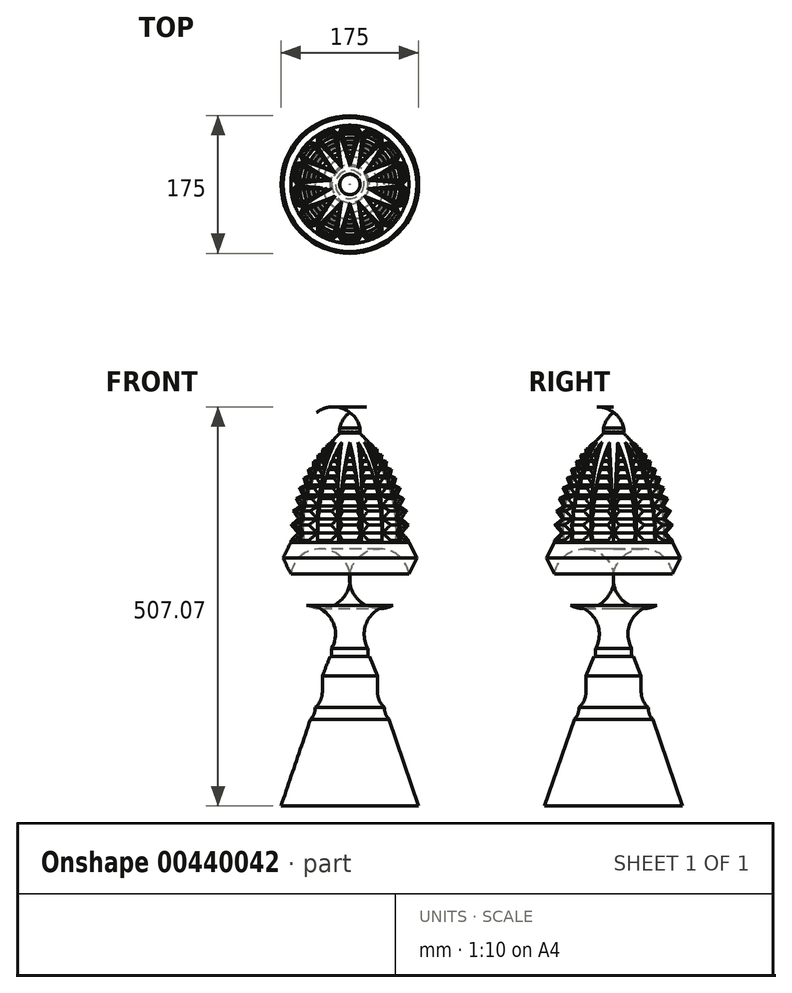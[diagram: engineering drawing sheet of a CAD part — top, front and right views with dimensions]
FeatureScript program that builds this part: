
annotation { "Feature Type Name" : "Feature", "Feature Type Description" : "" }
export const myFeature = defineFeature(function(context is Context, id is Id, definition is map)
    precondition{}
    {
        {
            var Q0;
            Q0=qCreatedBy(makeId("Front.planeOp"),FACE);
            var sketch = newSketch(context, id + "F0", { "sketchPlane" : qUnion([Q0])});
            skLineSegment(sketch, "E0", {"start": v(0, 0) * mm, "end": v(87.5, 0) * mm});
            skLineSegment(sketch, "E1", {"start": v(0, 0) * mm, "end": v(0, 110) * mm});
            skLineSegment(sketch, "E2", {"start": v(0, 110) * mm, "end": v(50, 110) * mm});
            skLineSegment(sketch, "E3", {"start": v(50, 110) * mm, "end": v(87.5, 0) * mm});
            skLineSegment(sketch, "E4", {"start": v(-407.4, 0) * mm, "end": v(-407.4, 108) * mm});
            skLineSegment(sketch, "E5", {"start": v(-453.78, 108) * mm, "end": v(-352.64, 108) * mm});
            skLineSegment(sketch, "E6", {"start": v(-407.4, 108) * mm, "end": v(-407.4, 123) * mm});
            skLineSegment(sketch, "E7", {"start": v(-407.4, 123) * mm, "end": v(-407.4, 143) * mm});
            skLineSegment(sketch, "E8", {"start": v(0, 110) * mm, "end": v(0, 125) * mm});
            skLineSegment(sketch, "E9", {"start": v(0, 125) * mm, "end": v(0, 145) * mm});
            skLineSegment(sketch, "E10", {"start": v(-446.66, 122.59) * mm, "end": v(-359.68, 122.59) * mm});
            skLineSegment(sketch, "E11", {"start": v(0, 125) * mm, "end": v(44, 125) * mm});
            skLineSegment(sketch, "E12", {"start": v(-438.63, 143) * mm, "end": v(-367.86, 143) * mm});
            skLineSegment(sketch, "E13", {"start": v(0, 145) * mm, "end": v(35, 145) * mm});
            skArc(sketch, "E14", {"start": v(35, 145) * mm, "mid": v(37.38, 134.05) * mm, "end": v(44, 125) * mm});
            skArc(sketch, "E15", {"start": v(44, 125) * mm, "mid": v(45.42, 116.87) * mm, "end": v(50, 110) * mm});
            skLineSegment(sketch, "E16", {"start": v(-407.4, 143) * mm, "end": v(-407.4, 188) * mm});
            skLineSegment(sketch, "E17", {"start": v(-378.97, 188) * mm, "end": v(-428.97, 188) * mm});
            skLineSegment(sketch, "E18", {"start": v(-407.4, 188) * mm, "end": v(-407.4, 198) * mm});
            skLineSegment(sketch, "E19", {"start": v(0, 145) * mm, "end": v(0, 190) * mm});
            skLineSegment(sketch, "E20", {"start": v(-437.68, 163) * mm, "end": v(-367.68, 163) * mm});
            skLineSegment(sketch, "E21", {"start": v(0, 165) * mm, "end": v(35, 165) * mm, "construction": true});
            skLineSegment(sketch, "E22", {"start": v(35, 165) * mm, "end": v(35, 145) * mm});
            skLineSegment(sketch, "E23", {"start": v(0, 190) * mm, "end": v(25, 190) * mm});
            skLineSegment(sketch, "E24", {"start": v(25, 190) * mm, "end": v(35, 165) * mm});
            skLineSegment(sketch, "E25", {"start": v(-407.4, 198) * mm, "end": v(-407.4, 253) * mm});
            skLineSegment(sketch, "E26", {"start": v(-458.35, 253) * mm, "end": v(-348.35, 253) * mm});
            skLineSegment(sketch, "E27", {"start": v(0, 190) * mm, "end": v(0, 200) * mm});
            skLineSegment(sketch, "E28", {"start": v(0, 200) * mm, "end": v(23, 200) * mm});
            skLineSegment(sketch, "E29", {"start": v(-407.4, 253) * mm, "end": v(-407.4, 263) * mm});
            skLineSegment(sketch, "E30", {"start": v(23, 200) * mm, "end": v(23, 190) * mm});
            skLineSegment(sketch, "E31", {"start": v(0, 200) * mm, "end": v(0, 255) * mm});
            skLineSegment(sketch, "E32", {"start": v(0, 255) * mm, "end": v(55, 255) * mm});
            skArc(sketch, "E33", {"start": v(55, 255) * mm, "mid": v(23.18, 236.7) * mm, "end": v(23, 200) * mm});
            skLineSegment(sketch, "E34", {"start": v(-407.4, 263) * mm, "end": v(-407.4, 500) * mm});
            skLineSegment(sketch, "E35", {"start": v(-479.16, 303) * mm, "end": v(-329.16, 303) * mm});
            skLineSegment(sketch, "E36", {"start": v(-489.2, 323) * mm, "end": v(-319.2, 323) * mm});
            skPoint(sketch, "E37", {"position": v(-407.4, 303) * mm});
            skPoint(sketch, "E37.positionSnap0", {"position": v(-404.16, 303) * mm});
            skPoint(sketch, "E38", {"position": v(-407.4, 323) * mm});
            skPoint(sketch, "E38.positionSnap0", {"position": v(-404.2, 323) * mm});
            skLineSegment(sketch, "E39", {"start": v(0, 255) * mm, "end": v(0, 295) * mm});
            skLineSegment(sketch, "E40", {"start": v(0, 295) * mm, "end": v(0, 315) * mm});
            skLineSegment(sketch, "E41", {"start": v(0, 315) * mm, "end": v(0, 335) * mm});
            skLineSegment(sketch, "E42", {"start": v(0, 335) * mm, "end": v(0, 475) * mm});
            skLineSegment(sketch, "E43", {"start": v(0, 295) * mm, "end": v(75, 295) * mm});
            skLineSegment(sketch, "E44", {"start": v(0, 315) * mm, "end": v(85, 315) * mm});
            skLineSegment(sketch, "E45", {"start": v(85, 315) * mm, "end": v(75, 295) * mm});
            skArc(sketch, "E46", {"start": v(55, 255) * mm, "mid": v(71.5, 271.75) * mm, "end": v(75, 295) * mm});
            skPoint(sketch, "E47", {"position": v(-407.4, 343) * mm});
            skLineSegment(sketch, "E48", {"start": v(-407.4, 343) * mm, "end": v(-407.4, 483) * mm});
            skLineSegment(sketch, "E49", {"start": v(-478.01, 343) * mm, "end": v(-328.5, 343) * mm});
            skLineSegment(sketch, "E50", {"start": v(0, 335) * mm, "end": v(75, 335) * mm});
            skLineSegment(sketch, "E51", {"start": v(75, 335) * mm, "end": v(85, 315) * mm});
            skLineSegment(sketch, "E52", {"start": v(-416.64, 483) * mm, "end": v(-390.64, 483) * mm});
            skLineSegment(sketch, "E53", {"start": v(0, 475) * mm, "end": v(13, 475) * mm});
            skArc(sketch, "E54", {"start": v(75, 335) * mm, "mid": v(60.65, 412.38) * mm, "end": v(13, 475) * mm});
            skLineSegment(sketch, "E55", {"start": v(0, 475) * mm, "end": v(0, 500) * mm});
            skLineSegment(sketch, "E56", {"start": v(13, 475) * mm, "end": v(13, 480) * mm});
            skLineSegment(sketch, "E57", {"start": v(13, 480) * mm, "end": v(0, 480) * mm});
            skArc(sketch, "E58", {"start": v(13, 480) * mm, "mid": v(8.26, 491.14) * mm, "end": v(0, 500) * mm});
            skSolve(sketch);
        }
        {
            var Q0;
            {var subQ2=sQuery(id+"F0.wireOp",EDGE,"E57");Q0=makeQuery(id+"F0.imprint","IMPRINT",FACE,{"disambiguationData":[TD([[makeQuery(id+"F0.imprint","IMPRINT",EDGE,{"derivedFrom":subQ2}),-1.0]])]});}
            var Q1;
            Q1=makeQuery(id+"F0.imprint","IMPRINT",FACE,{"disambiguationData":[TD([[makeQuery(id+"F0.imprint","IMPRINT",EDGE,{"derivedFrom":sQuery(id+"F0.wireOp",EDGE,"E41")}),-1.0]])]});
            var Q2;
            Q2=makeQuery(id+"F0.imprint","IMPRINT",FACE,{"disambiguationData":[TD([[makeQuery(id+"F0.imprint","IMPRINT",EDGE,{"derivedFrom":sQuery(id+"F0.wireOp",EDGE,"E32")}),1.0]])]});
            var Q3;
            {var subQ0=sQuery(id+"F0.wireOp",EDGE,"E53");Q3=makeQuery(id+"F0.imprint","IMPRINT",FACE,{"disambiguationData":[TD([[makeQuery(id+"F0.imprint","IMPRINT",EDGE,{"derivedFrom":subQ0}),1.0]])]});}
            var Q4;
            Q4=makeQuery(id+"F0.imprint","IMPRINT",FACE,{"disambiguationData":[TD([[makeQuery(id+"F0.imprint","IMPRINT",EDGE,{"derivedFrom":sQuery(id+"F0.wireOp",EDGE,"E0")}),1.0]])]});
            var Q5;
            Q5=makeQuery(id+"F0.imprint","IMPRINT",FACE,{"disambiguationData":[TD([[makeQuery(id+"F0.imprint","IMPRINT",EDGE,{"derivedFrom":sQuery(id+"F0.wireOp",EDGE,"E9")}),-1.0]])]});
            var Q6;
            Q6=makeQuery(id+"F0.imprint","IMPRINT",FACE,{"disambiguationData":[TD([[makeQuery(id+"F0.imprint","IMPRINT",EDGE,{"derivedFrom":sQuery(id+"F0.wireOp",EDGE,"E13")}),1.0]])]});
            var Q7;
            {var subQ0=sQuery(id+"F0.wireOp",EDGE,"E27");Q7=makeQuery(id+"F0.imprint","IMPRINT",FACE,{"disambiguationData":[TD([[makeQuery(id+"F0.imprint","IMPRINT",EDGE,{"derivedFrom":subQ0}),-1.0]])]});}
            var Q8;
            Q8=makeQuery(id+"F0.imprint","IMPRINT",FACE,{"disambiguationData":[TD([[makeQuery(id+"F0.imprint","IMPRINT",EDGE,{"derivedFrom":sQuery(id+"F0.wireOp",EDGE,"E42")}),-1.0]])]});
            var Q9;
            Q9=makeQuery(id+"F0.imprint","IMPRINT",FACE,{"disambiguationData":[TD([[makeQuery(id+"F0.imprint","IMPRINT",EDGE,{"derivedFrom":sQuery(id+"F0.wireOp",EDGE,"E2")}),1.0]])]});
            var Q10;
            Q10=makeQuery(id+"F0.imprint","IMPRINT",FACE,{"disambiguationData":[TD([[makeQuery(id+"F0.imprint","IMPRINT",EDGE,{"derivedFrom":sQuery(id+"F0.wireOp",EDGE,"E28")}),1.0]])]});
            var Q11;
            Q11=makeQuery(id+"F0.imprint","IMPRINT",FACE,{"disambiguationData":[TD([[makeQuery(id+"F0.imprint","IMPRINT",EDGE,{"derivedFrom":sQuery(id+"F0.wireOp",EDGE,"E40")}),-1.0]])]});
            var Q12;
            Q12=sQuery(id+"F0.wireOp",EDGE,"E1");
            revolve(context, id + "F1", {"entities" : qUnion([Q0, Q1, Q2, Q3, Q4, Q5, Q6, Q7, Q8, Q9, Q10, Q11]), "axis" : qUnion([Q12]), "revolveType" : RevolveType.FULL});
        }
        {
            var Q0;
            Q0=qCreatedBy(makeId("Front.planeOp"),FACE);
            var sketch = newSketch(context, id + "F2", { "sketchPlane" : qUnion([Q0])});
            skLineSegment(sketch, "E59.0", {"start": v(75, 335) * mm, "end": v(-75, 335) * mm});
            skArc(sketch, "E60.0", {"start": v(75, 335) * mm, "mid": v(60.65, 412.38) * mm, "end": v(13, 475) * mm});
            skArc(sketch, "E61.0", {"start": v(65, 335) * mm, "mid": v(52.46, 409.36) * mm, "end": v(8.98, 470.97) * mm});
            skPoint(sketch, "E62", {"position": v(65, 335) * mm});
            skPoint(sketch, "E63", {"position": v(65.1, 337) * mm});
            skLineSegment(sketch, "E64", {"start": v(65.1, 337) * mm, "end": v(75.18, 347.14) * mm});
            skLineSegment(sketch, "E65", {"start": v(75.18, 347.14) * mm, "end": v(64.82, 357) * mm});
            skPoint(sketch, "E66", {"position": v(64.66, 359) * mm});
            skLineSegment(sketch, "E67", {"start": v(64.66, 359) * mm, "end": v(73.25, 369.28) * mm});
            skLineSegment(sketch, "E68", {"start": v(73.25, 369.28) * mm, "end": v(62.19, 376.83) * mm});
            skLineSegment(sketch, "E69", {"start": v(61.8, 378.8) * mm, "end": v(69.05, 388.9) * mm});
            skLineSegment(sketch, "E70", {"start": v(69.05, 388.9) * mm, "end": v(57.85, 394.3) * mm});
            skLineSegment(sketch, "E71", {"start": v(57.25, 396.2) * mm, "end": v(63.37, 405.89) * mm});
            skLineSegment(sketch, "E72", {"start": v(63.37, 405.89) * mm, "end": v(52.46, 409.36) * mm});
            skLineSegment(sketch, "E73", {"start": v(51.68, 411.2) * mm, "end": v(56.91, 420.27) * mm});
            skLineSegment(sketch, "E74", {"start": v(56.91, 420.27) * mm, "end": v(46.6, 422.07) * mm});
            skLineSegment(sketch, "E75", {"start": v(45.67, 423.85) * mm, "end": v(50.27, 432.19) * mm});
            skLineSegment(sketch, "E76", {"start": v(50.27, 432.19) * mm, "end": v(40.75, 432.55) * mm});
            skLineSegment(sketch, "E77", {"start": v(39.7, 434.26) * mm, "end": v(43.94, 441.8) * mm});
            skLineSegment(sketch, "E78", {"start": v(43.94, 441.8) * mm, "end": v(35.33, 440.95) * mm});
            skLineSegment(sketch, "E79", {"start": v(34.19, 442.6) * mm, "end": v(38.3, 449.32) * mm});
            skLineSegment(sketch, "E80", {"start": v(38.3, 449.32) * mm, "end": v(30.64, 447.44) * mm});
            skLineSegment(sketch, "E81", {"start": v(29.42, 449.02) * mm, "end": v(33.63, 454.93) * mm});
            skLineSegment(sketch, "E82", {"start": v(33.63, 454.93) * mm, "end": v(26.93, 452.15) * mm, "construction": true});
            skSolve(sketch);
        }
        {
            var Q0;
            Q0=qCreatedBy(makeId("Front.planeOp"),FACE);
            var sketch = newSketch(context, id + "F3", { "sketchPlane" : qUnion([Q0])});
            skArc(sketch, "E83.0", {"start": v(75, 335) * mm, "mid": v(60.65, 412.38) * mm, "end": v(13, 475) * mm});
            skLineSegment(sketch, "E84.0", {"start": v(0, 335) * mm, "end": v(75, 335) * mm});
            skLineSegment(sketch, "E85.0", {"start": v(0, 475) * mm, "end": v(13, 475) * mm});
            skArc(sketch, "E86.0", {"start": v(65, 335) * mm, "mid": v(54.28, 411.28) * mm, "end": v(11, 475) * mm});
            skPoint(sketch, "E87", {"position": v(65, 335) * mm});
            skLineSegment(sketch, "E88", {"start": v(65.64, 346.81) * mm, "end": v(75.09, 337) * mm});
            skLineSegment(sketch, "E89", {"start": v(65.64, 346.81) * mm, "end": v(74.68, 357) * mm});
            skLineSegment(sketch, "E90", {"start": v(74.68, 357) * mm, "end": v(65.04, 364.8) * mm});
            skLineSegment(sketch, "E91", {"start": v(65.04, 364.8) * mm, "end": v(72.3, 374.84) * mm});
            skLineSegment(sketch, "E92", {"start": v(72.3, 374.84) * mm, "end": v(62.87, 380.83) * mm});
            skLineSegment(sketch, "E93", {"start": v(62.87, 380.83) * mm, "end": v(68.62, 390.41) * mm});
            skLineSegment(sketch, "E94", {"start": v(68.62, 390.41) * mm, "end": v(59.68, 394.82) * mm});
            skLineSegment(sketch, "E95", {"start": v(59.68, 394.82) * mm, "end": v(64.21, 403.7) * mm});
            skLineSegment(sketch, "E96", {"start": v(64.21, 403.7) * mm, "end": v(55.63, 407.65) * mm});
            skLineSegment(sketch, "E97", {"start": v(55.63, 407.65) * mm, "end": v(58.72, 416.58) * mm});
            skLineSegment(sketch, "E98", {"start": v(58.72, 416.58) * mm, "end": v(50.95, 419.3) * mm});
            skLineSegment(sketch, "E99", {"start": v(50.95, 419.3) * mm, "end": v(53.19, 427.23) * mm});
            skLineSegment(sketch, "E100", {"start": v(53.19, 427.23) * mm, "end": v(45.85, 429.77) * mm});
            skLineSegment(sketch, "E101", {"start": v(45.85, 429.77) * mm, "end": v(46.92, 437.46) * mm});
            skLineSegment(sketch, "E102", {"start": v(46.92, 437.46) * mm, "end": v(40.53, 439.07) * mm});
            skLineSegment(sketch, "E103", {"start": v(40.53, 439.07) * mm, "end": v(41.15, 445.63) * mm});
            skLineSegment(sketch, "E104", {"start": v(41.15, 445.63) * mm, "end": v(35.18, 447.26) * mm});
            skLineSegment(sketch, "E105", {"start": v(35.18, 447.26) * mm, "end": v(34.91, 453.44) * mm});
            skLineSegment(sketch, "E106", {"start": v(34.91, 453.44) * mm, "end": v(29.94, 454.37) * mm});
            skLineSegment(sketch, "E107", {"start": v(29.94, 454.37) * mm, "end": v(29.6, 459.42) * mm});
            skLineSegment(sketch, "E108", {"start": v(29.6, 459.42) * mm, "end": v(24.96, 460.49) * mm});
            skLineSegment(sketch, "E109", {"start": v(24.96, 460.49) * mm, "end": v(24, 465.14) * mm, "construction": true});
            skLineSegment(sketch, "E110", {"start": v(0, 475) * mm, "end": v(0, 335) * mm});
            skSolve(sketch);
        }
        {
            var Q0;
            {var subQ0=sQuery(id+"F3.wireOp",EDGE,"E96");Q0=makeQuery(id+"F3.imprint","IMPRINT",FACE,{"disambiguationData":[TD([[makeQuery(id+"F3.imprint","IMPRINT",EDGE,{"derivedFrom":subQ0}),-1.0]])]});}
            var Q1;
            {var subQ0=sQuery(id+"F3.wireOp",EDGE,"E88");Q1=makeQuery(id+"F3.imprint","IMPRINT",FACE,{"disambiguationData":[TD([[makeQuery(id+"F3.imprint","IMPRINT",EDGE,{"derivedFrom":subQ0}),1.0]])]});}
            var Q2;
            {var subQ0=sQuery(id+"F3.wireOp",EDGE,"E90");Q2=makeQuery(id+"F3.imprint","IMPRINT",FACE,{"disambiguationData":[TD([[makeQuery(id+"F3.imprint","IMPRINT",EDGE,{"derivedFrom":subQ0}),-1.0]])]});}
            var Q3;
            {var subQ0=sQuery(id+"F3.wireOp",EDGE,"E102");Q3=makeQuery(id+"F3.imprint","IMPRINT",FACE,{"disambiguationData":[TD([[makeQuery(id+"F3.imprint","IMPRINT",EDGE,{"derivedFrom":subQ0}),-1.0]])]});}
            var Q4;
            {var subQ0=sQuery(id+"F3.wireOp",EDGE,"E106");Q4=makeQuery(id+"F3.imprint","IMPRINT",FACE,{"disambiguationData":[TD([[makeQuery(id+"F3.imprint","IMPRINT",EDGE,{"derivedFrom":subQ0}),-1.0]])]});}
            var Q5;
            {var subQ0=sQuery(id+"F3.wireOp",EDGE,"E92");Q5=makeQuery(id+"F3.imprint","IMPRINT",FACE,{"disambiguationData":[TD([[makeQuery(id+"F3.imprint","IMPRINT",EDGE,{"derivedFrom":subQ0}),-1.0]])]});}
            var Q6;
            {var subQ0=sQuery(id+"F3.wireOp",EDGE,"E94");Q6=makeQuery(id+"F3.imprint","IMPRINT",FACE,{"disambiguationData":[TD([[makeQuery(id+"F3.imprint","IMPRINT",EDGE,{"derivedFrom":subQ0}),-1.0]])]});}
            var Q7;
            {var subQ0=sQuery(id+"F3.wireOp",EDGE,"E100");Q7=makeQuery(id+"F3.imprint","IMPRINT",FACE,{"disambiguationData":[TD([[makeQuery(id+"F3.imprint","IMPRINT",EDGE,{"derivedFrom":subQ0}),-1.0]])]});}
            var Q8;
            {var subQ0=sQuery(id+"F3.wireOp",EDGE,"E104");Q8=makeQuery(id+"F3.imprint","IMPRINT",FACE,{"disambiguationData":[TD([[makeQuery(id+"F3.imprint","IMPRINT",EDGE,{"derivedFrom":subQ0}),-1.0]])]});}
            var Q9;
            {var subQ0=sQuery(id+"F3.wireOp",EDGE,"E98");Q9=makeQuery(id+"F3.imprint","IMPRINT",FACE,{"disambiguationData":[TD([[makeQuery(id+"F3.imprint","IMPRINT",EDGE,{"derivedFrom":subQ0}),-1.0]])]});}
            var Q10;
            Q10=sQuery(id+"F0.wireOp",EDGE,"E1");
            revolve(context, id + "F4", {"operationType" : NewBodyOperationType.REMOVE, "entities" : qUnion([Q0, Q1, Q2, Q3, Q4, Q5, Q6, Q7, Q8, Q9]), "axis" : qUnion([Q10]), "revolveType" : RevolveType.FULL, "oppositeDirection" : true});
        }
        {
            var Q0;
            Q0=makeQuery(id+"F1.opRevolve","SWEPT_EDGE",EDGE,{"disambiguationData":[OSD([sQuery(id+"F0.wireOp",EDGE,"E50"),sQuery(id+"F0.wireOp",EDGE,"E51"),sQuery(id+"F0.wireOp",EDGE,"E54")])]});
            var Q1;
            Q1=sQuery(id+"F0.wireOp",VERTEX,"E42.start");
            cPlane(context, id + "F5", {"entities" : qUnion([Q0, Q1]), "cplaneType" : CPlaneType.LINE_POINT, "offset" : 25 * mm, "width" : 150 * mm, "height" : 150 * mm});
        }
        {
            var Q0;
            Q0=qCreatedBy(id+"F5.planeOp",FACE);
            var sketch = newSketch(context, id + "F6", { "sketchPlane" : qUnion([Q0])});
            skLineSegment(sketch, "E111", {"start": v(75, 0) * mm, "end": v(75, -7.5) * mm});
            skLineSegment(sketch, "E112", {"start": v(75, -7.5) * mm, "end": v(65, 0) * mm});
            skLineSegment(sketch, "E113", {"start": v(65, 0) * mm, "end": v(75, 7.5) * mm});
            skLineSegment(sketch, "E114", {"start": v(75, 7.5) * mm, "end": v(75, 0) * mm});
            skLineSegment(sketch, "E115.0", {"start": v(0, 0) * mm, "end": v(75, 0) * mm});
            skSolve(sketch);
        }
        {
            var Q0;
            {var subQ0=sQuery(id+"F6.wireOp",EDGE,"E111");Q0=makeQuery(id+"F6.imprint","IMPRINT",FACE,{"disambiguationData":[TD([[makeQuery(id+"F6.imprint","IMPRINT",EDGE,{"derivedFrom":subQ0}),-1.0]])]});}
            var Q1;
            {var subQ0=sQuery(id+"F6.wireOp",EDGE,"E113");Q1=makeQuery(id+"F6.imprint","IMPRINT",FACE,{"disambiguationData":[TD([[makeQuery(id+"F6.imprint","IMPRINT",EDGE,{"derivedFrom":subQ0}),-1.0]])]});}
            var Q2;
            Q2=sQuery(id+"F0.wireOp",EDGE,"E54");
            sweep(context, id + "F7", {"profiles" : qUnion([Q0, Q1]), "path" : qUnion([Q2])});
        }
        {
            var Q0;
            Q0=makeQuery(id+"F7.opSweep","SWEPT_BODY",BODY,{"disambiguationData":[OSD([sQuery(id+"F0.wireOp",EDGE,"E54"),sQuery(id+"F6.wireOp",EDGE,"E111"),sQuery(id+"F6.wireOp",EDGE,"E112"),sQuery(id+"F6.wireOp",EDGE,"E113"),sQuery(id+"F6.wireOp",EDGE,"E114")])]});
            var Q1;
            Q1=sQuery(id+"F0.wireOp",EDGE,"E42");
            circularPattern(context, id + "F8", {"operationType" : NewBodyOperationType.REMOVE, "entities" : qUnion([Q0]), "axis" : qUnion([Q1]), "angle" : 360 * degree, "instanceCount" : 14, "equalSpace" : true});
        }
        {
            var Q0;
            {var subQ8=sQuery(id+"F3.wireOp",EDGE,"E110");Q0=makeQuery(id+"F3.imprint","IMPRINT",FACE,{"disambiguationData":[TD([[makeQuery(id+"F3.imprint","IMPRINT",EDGE,{"derivedFrom":subQ8}),1.0]])]});}
            var Q1;
            Q1=sQuery(id+"F3.wireOp",EDGE,"E110");
            revolve(context, id + "F9", {"operationType" : NewBodyOperationType.ADD, "entities" : qUnion([Q0]), "axis" : qUnion([Q1]), "revolveType" : RevolveType.FULL});
        }
        {
            var Q0;
            Q0=makeQuery(id+"F8.boolean.opBoolean","COPY",FACE,{"derivedFrom":makeQuery(id+"F8.opPattern","COPY",FACE,{"derivedFrom":makeQuery(id+"F7.opSweep","CAP_FACE",FACE,{"disambiguationData":[OSD([sQuery(id+"F0.wireOp",VERTEX,"E54.start"),sQuery(id+"F6.wireOp",EDGE,"E111"),sQuery(id+"F6.wireOp",EDGE,"E112"),sQuery(id+"F6.wireOp",EDGE,"E113"),sQuery(id+"F6.wireOp",EDGE,"E114")])],"isStart":true}),"instanceName":"7"})});
            cPlane(context, id + "F10", {"entities" : qUnion([Q0]), "cplaneType" : CPlaneType.OFFSET, "offset" : 165 * mm, "width" : 150 * mm, "height" : 150 * mm});
        }
        {
            var Q0;
            Q0=qCreatedBy(id+"F10.planeOp",FACE);
            var sketch = newSketch(context, id + "F11", { "sketchPlane" : qUnion([Q0])});
            skCircle(sketch, "E116.0", {"center": v(0, 0) * mm, "radius": 13 * mm});
            skCircle(sketch, "E117.0", {"center": v(0, 0) * mm, "radius": 15 * mm});
            skSolve(sketch);
        }
        {
            var Q0;
            Q0=makeQuery(id+"F11.imprint","IMPRINT",FACE,{"disambiguationData":[TD([[makeQuery(id+"F11.imprint","IMPRINT",EDGE,{"derivedFrom":sQuery(id+"F11.wireOp",EDGE,"E116.0")}),-1.0]])]});
            extrude(context, id + "F12", {"entities" : qUnion([Q0]), "operationType" : NewBodyOperationType.REMOVE, "endBound" : BoundingType.UP_TO_NEXT, "oppositeDirection" : true, "depth" : 25 * mm, "offsetDistance" : 25 * mm});
        }
    });
